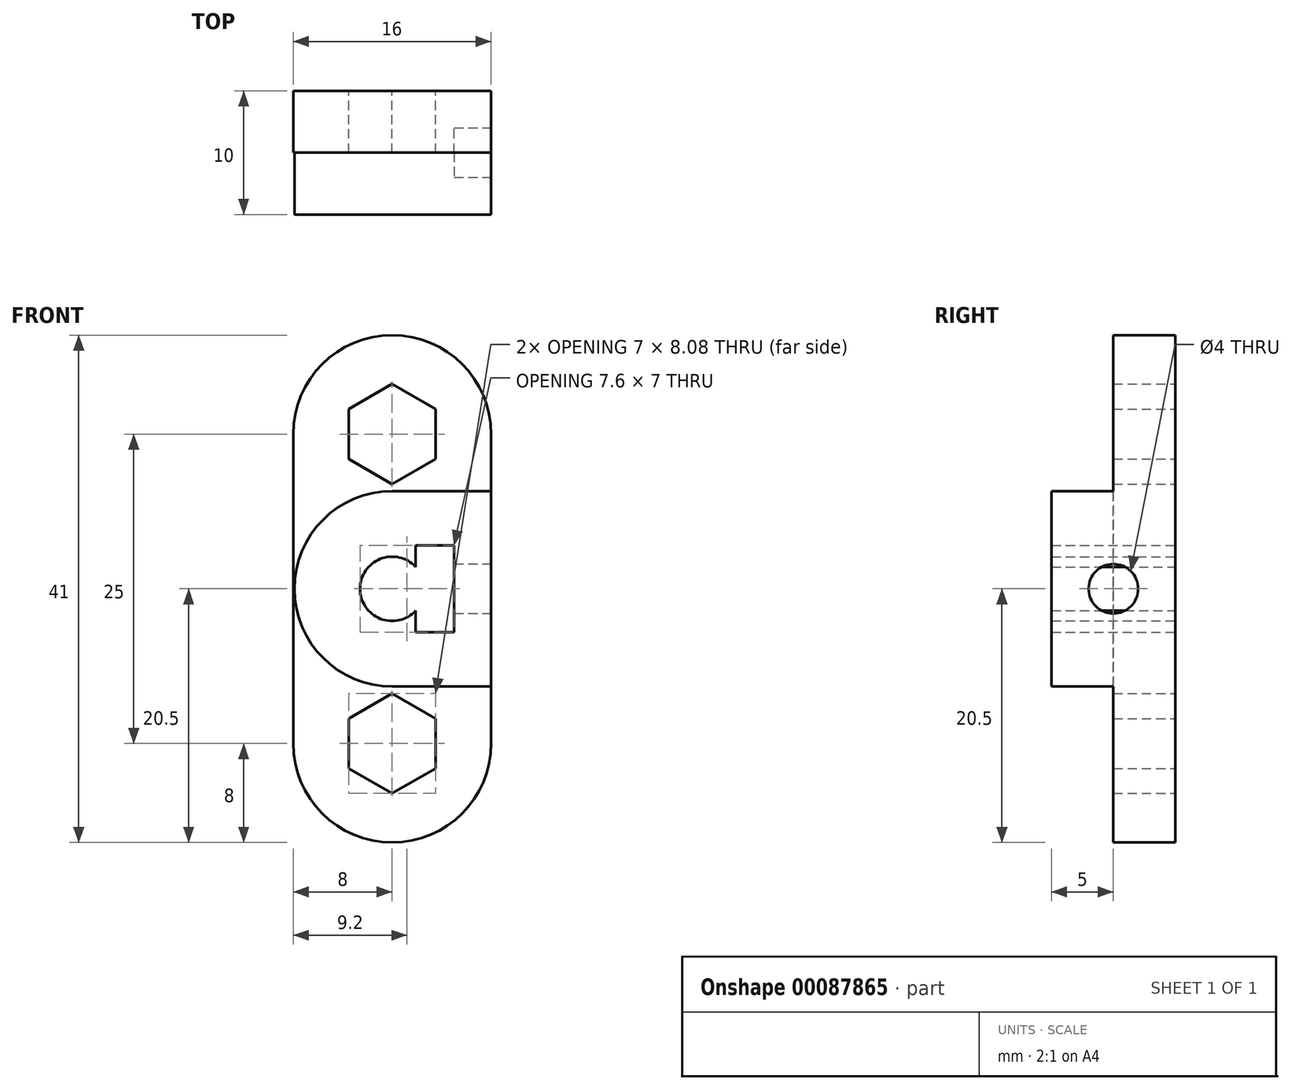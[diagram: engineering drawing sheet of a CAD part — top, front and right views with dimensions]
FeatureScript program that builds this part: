
annotation { "Feature Type Name" : "Feature", "Feature Type Description" : "" }
export const myFeature = defineFeature(function(context is Context, id is Id, definition is map)
    precondition{}
    {
        {
            var Q0;
            Q0=qCreatedBy(makeId("Front.planeOp"),FACE);
            var sketch = newSketch(context, id + "F0", { "sketchPlane" : qUnion([Q0])});
            skLineSegment(sketch, "E0.bottom", {"start": v(8, -12.5) * mm, "end": v(-8, -12.5) * mm, "construction": true});
            skLineSegment(sketch, "E0.top", {"start": v(8, 12.5) * mm, "end": v(-8, 12.5) * mm, "construction": true});
            skLineSegment(sketch, "E0.left", {"start": v(8, -12.5) * mm, "end": v(8, 12.5) * mm});
            skLineSegment(sketch, "E0.right", {"start": v(-8, -12.5) * mm, "end": v(-8, 12.5) * mm});
            skPoint(sketch, "E0.middle", {"position": v(0, 0) * mm});
            skArc(sketch, "E1", {"start": v(8, 12.5) * mm, "mid": v(0, 20.5) * mm, "end": v(-8, 12.5) * mm});
            skArc(sketch, "E2", {"start": v(-8, -12.5) * mm, "mid": v(0, -20.5) * mm, "end": v(8, -12.5) * mm});
            skCircle(sketch, "E3.cCircle", {"center": v(0, 12.5) * mm, "radius": 3.5 * mm, "construction": true});
            skLineSegment(sketch, "E3.0", {"start": v(3.5, 14.52) * mm, "end": v(3.5, 10.48) * mm});
            skLineSegment(sketch, "E3.1", {"start": v(3.5, 10.48) * mm, "end": v(0, 8.46) * mm});
            skLineSegment(sketch, "E3.2", {"start": v(0, 8.46) * mm, "end": v(-3.5, 10.48) * mm});
            skLineSegment(sketch, "E3.3", {"start": v(-3.5, 10.48) * mm, "end": v(-3.5, 14.52) * mm});
            skLineSegment(sketch, "E3.4", {"start": v(-3.5, 14.52) * mm, "end": v(0, 16.54) * mm});
            skLineSegment(sketch, "E3.5", {"start": v(0, 16.54) * mm, "end": v(3.5, 14.52) * mm});
            skPoint(sketch, "E3.0.midPoint", {"position": v(3.5, 12.5) * mm});
            skCircle(sketch, "E4.cCircle", {"center": v(0, -12.5) * mm, "radius": 3.5 * mm, "construction": true});
            skLineSegment(sketch, "E4.0", {"start": v(3.5, -10.48) * mm, "end": v(3.5, -14.52) * mm});
            skLineSegment(sketch, "E4.1", {"start": v(3.5, -14.52) * mm, "end": v(0, -16.54) * mm});
            skLineSegment(sketch, "E4.2", {"start": v(0, -16.54) * mm, "end": v(-3.5, -14.52) * mm});
            skLineSegment(sketch, "E4.3", {"start": v(-3.5, -14.52) * mm, "end": v(-3.5, -10.48) * mm});
            skLineSegment(sketch, "E4.4", {"start": v(-3.5, -10.48) * mm, "end": v(0, -8.46) * mm});
            skLineSegment(sketch, "E4.5", {"start": v(0, -8.46) * mm, "end": v(3.5, -10.48) * mm});
            skPoint(sketch, "E4.0.midPoint", {"position": v(3.5, -12.5) * mm});
            skArc(sketch, "E5", {"start": v(1.9, 1.77) * mm, "mid": v(-2.6, 0) * mm, "end": v(1.9, -1.77) * mm});
            skLineSegment(sketch, "E6.bottom", {"start": v(5, -3.5) * mm, "end": v(1.9, -3.5) * mm});
            skLineSegment(sketch, "E6.top", {"start": v(5, 3.5) * mm, "end": v(1.9, 3.5) * mm});
            skLineSegment(sketch, "E6.left", {"start": v(5, -3.5) * mm, "end": v(5, 3.5) * mm});
            skLineSegment(sketch, "E6.right", {"start": v(1.9, -3.5) * mm, "end": v(1.9, -1.77) * mm});
            skPoint(sketch, "E6.middle", {"position": v(3.45, 0) * mm});
            skLineSegment(sketch, "E7", {"start": v(3.45, 0) * mm, "end": v(-2.6, 0) * mm, "construction": true});
            skLineSegment(sketch, "E8.trimOffspring", {"start": v(1.9, 1.77) * mm, "end": v(1.9, 3.5) * mm});
            skSolve(sketch);
        }
        {
            var Q0;
            Q0 = qSketchRegion(id + "F0", true);
            extrude(context, id + "F1", {"entities" : qUnion([Q0]), "depth" : 5 * mm});
        }
        {
            var Q0;
            Q0=makeQuery(id+"F1.opExtrude","CAP_FACE",FACE,{"disambiguationData":[OSD([sQuery(id+"F0.wireOp",EDGE,"E0.left"),sQuery(id+"F0.wireOp",EDGE,"E0.right"),sQuery(id+"F0.wireOp",EDGE,"E1"),sQuery(id+"F0.wireOp",EDGE,"E2"),sQuery(id+"F0.wireOp",EDGE,"E3.0"),sQuery(id+"F0.wireOp",EDGE,"E3.1"),sQuery(id+"F0.wireOp",EDGE,"E3.2"),sQuery(id+"F0.wireOp",EDGE,"E3.3"),sQuery(id+"F0.wireOp",EDGE,"E3.4"),sQuery(id+"F0.wireOp",EDGE,"E3.5"),sQuery(id+"F0.wireOp",EDGE,"E4.0"),sQuery(id+"F0.wireOp",EDGE,"E4.1"),sQuery(id+"F0.wireOp",EDGE,"E4.2"),sQuery(id+"F0.wireOp",EDGE,"E4.3"),sQuery(id+"F0.wireOp",EDGE,"E4.4"),sQuery(id+"F0.wireOp",EDGE,"E4.5"),sQuery(id+"F0.wireOp",EDGE,"E5"),sQuery(id+"F0.wireOp",EDGE,"E6.bottom"),sQuery(id+"F0.wireOp",EDGE,"E6.top"),sQuery(id+"F0.wireOp",EDGE,"E6.left"),sQuery(id+"F0.wireOp",EDGE,"E6.right"),sQuery(id+"F0.wireOp",EDGE,"E8.trimOffspring")])],"isStart":false});
            var sketch = newSketch(context, id + "F2", { "sketchPlane" : qUnion([Q0])});
            skLineSegment(sketch, "E9", {"start": v(0, -8.46) * mm, "end": v(0, 8.46) * mm, "construction": true});
            skLineSegment(sketch, "E10", {"start": v(0, 8.46) * mm, "end": v(-8, 0) * mm, "construction": true});
            skLineSegment(sketch, "E11", {"start": v(-8, 0) * mm, "end": v(0, 0) * mm, "construction": true});
            skArc(sketch, "E12", {"start": v(0, 7.9) * mm, "mid": v(-7.9, 0) * mm, "end": v(0, -7.9) * mm});
            skLineSegment(sketch, "E13", {"start": v(8, -7.9) * mm, "end": v(0, -7.9) * mm});
            skLineSegment(sketch, "E14", {"start": v(8, 7.9) * mm, "end": v(0, 7.9) * mm});
            skArc(sketch, "E15.0", {"start": v(1.9, 1.77) * mm, "mid": v(-2.6, 0) * mm, "end": v(1.9, -1.77) * mm});
            skLineSegment(sketch, "E16.0", {"start": v(1.9, 1.77) * mm, "end": v(1.9, 3.5) * mm});
            skLineSegment(sketch, "E17.0", {"start": v(5, -3.5) * mm, "end": v(5, 3.5) * mm});
            skLineSegment(sketch, "E18.0", {"start": v(1.9, -3.5) * mm, "end": v(1.9, -1.77) * mm});
            skLineSegment(sketch, "E19.0", {"start": v(5, -3.5) * mm, "end": v(1.9, -3.5) * mm});
            skLineSegment(sketch, "E20.0", {"start": v(5, 3.5) * mm, "end": v(1.9, 3.5) * mm});
            skSolve(sketch);
        }
        {
            var Q0;
            Q0=makeQuery(id+"F2.imprint","IMPRINT",FACE,{"disambiguationData":[TD([[makeQuery(id+"F2.imprint","IMPRINT",EDGE,{"derivedFrom":sQuery(id+"F2.wireOp",EDGE,"E12")}),1.0]])]});
            extrude(context, id + "F3", {"entities" : qUnion([Q0]), "operationType" : NewBodyOperationType.ADD, "depth" : 5 * mm});
        }
        {
            var Q0;
            {var subQ0=sQuery(id+"F0.wireOp",EDGE,"E0.left");Q0=makeQuery(id+"F3.boolean.opBoolean","MERGE",FACE,{"derivedFrom":[makeQuery(id+"F1.opExtrude","SWEPT_FACE",FACE,{"disambiguationData":[OSD([subQ0])]}),makeQuery(id+"F3.opExtrude","SWEPT_FACE",FACE,{"disambiguationData":[OSD([subQ0])]})]});}
            var sketch = newSketch(context, id + "F4", { "sketchPlane" : qUnion([Q0])});
            skLineSegment(sketch, "E21", {"start": v(-10, 0) * mm, "end": v(0, 0) * mm, "construction": true});
            skLineSegment(sketch, "E22", {"start": v(-5, -7.9) * mm, "end": v(-5, 7.9) * mm, "construction": true});
            skCircle(sketch, "E23", {"center": v(-5, 0) * mm, "radius": 2 * mm});
            skSolve(sketch);
        }
        {
            var Q0;
            Q0=makeQuery(id+"F4.imprint","IMPRINT",FACE,{"disambiguationData":[TD([[makeQuery(id+"F4.imprint","IMPRINT",EDGE,{"derivedFrom":sQuery(id+"F4.wireOp",EDGE,"E23")}),1.0]])]});
            var Q1;
            Q1=makeQuery(id+"F3.boolean.opBoolean","MERGE",FACE,{"derivedFrom":[makeQuery(id+"F1.opExtrude","SWEPT_FACE",FACE,{"disambiguationData":[OSD([sQuery(id+"F0.wireOp",EDGE,"E6.right")])]}),makeQuery(id+"F3.opExtrude","SWEPT_FACE",FACE,{"disambiguationData":[OSD([sQuery(id+"F2.wireOp",EDGE,"E18.0")])]})]});
            extrude(context, id + "F5", {"entities" : qUnion([Q0]), "operationType" : NewBodyOperationType.REMOVE, "endBound" : BoundingType.UP_TO_SURFACE, "oppositeDirection" : true, "endBoundEntityFace" : qUnion([Q1]), "depth" : 25 * mm});
        }
    });
